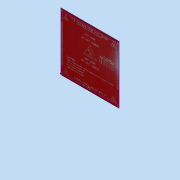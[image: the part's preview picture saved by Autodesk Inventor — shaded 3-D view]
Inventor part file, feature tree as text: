
AUTODESK INVENTOR PART (.ipt)
format: ipt  version: 2015 (Build 190159000, 159)  size: 128,000 bytes
history: native  units: in
note: dims shown in document units (in); Inventor stores cm internally (conversion verified against a paired STEP export)
features: sketch x3, extrude x1, hole x1, other x1
ambient origin geometry x8: Origin, YZ Plane, XZ Plane, XY Plane, X Axis, Y Axis, Z Axis, Center Point
bodies: Solid1 (feature_tree)
feature tree (6):
  extrude  "Extrusion1"  Depth=8.4252in
  sketch  "Sketch4"  dims[d4=0.065in d5=0.0in d41=0.1181in]
  hole  "Hole1"  [1 undecoded]
  sketch  "Sketch3"  dims[d2=8.4252in d3=8.4252in]
  other  "Image2"
  sketch  "Sketch5"  dims[d42=0.1181in d43=0.1181in d44=0.1181in d45=0.1181in d46=0.1181in d47=0.1181in d48=0.1181in d49=0.1181in d50=0.75in d51=0.375in d52=0.25in d53=0.5635in d54=1.0in d55=0.8108in]
note: 1 required parameter value undecoded (feature->parameter linkage not recoverable at this tier; creation-order binding heuristic only, values carry confidence <= 0.55)
